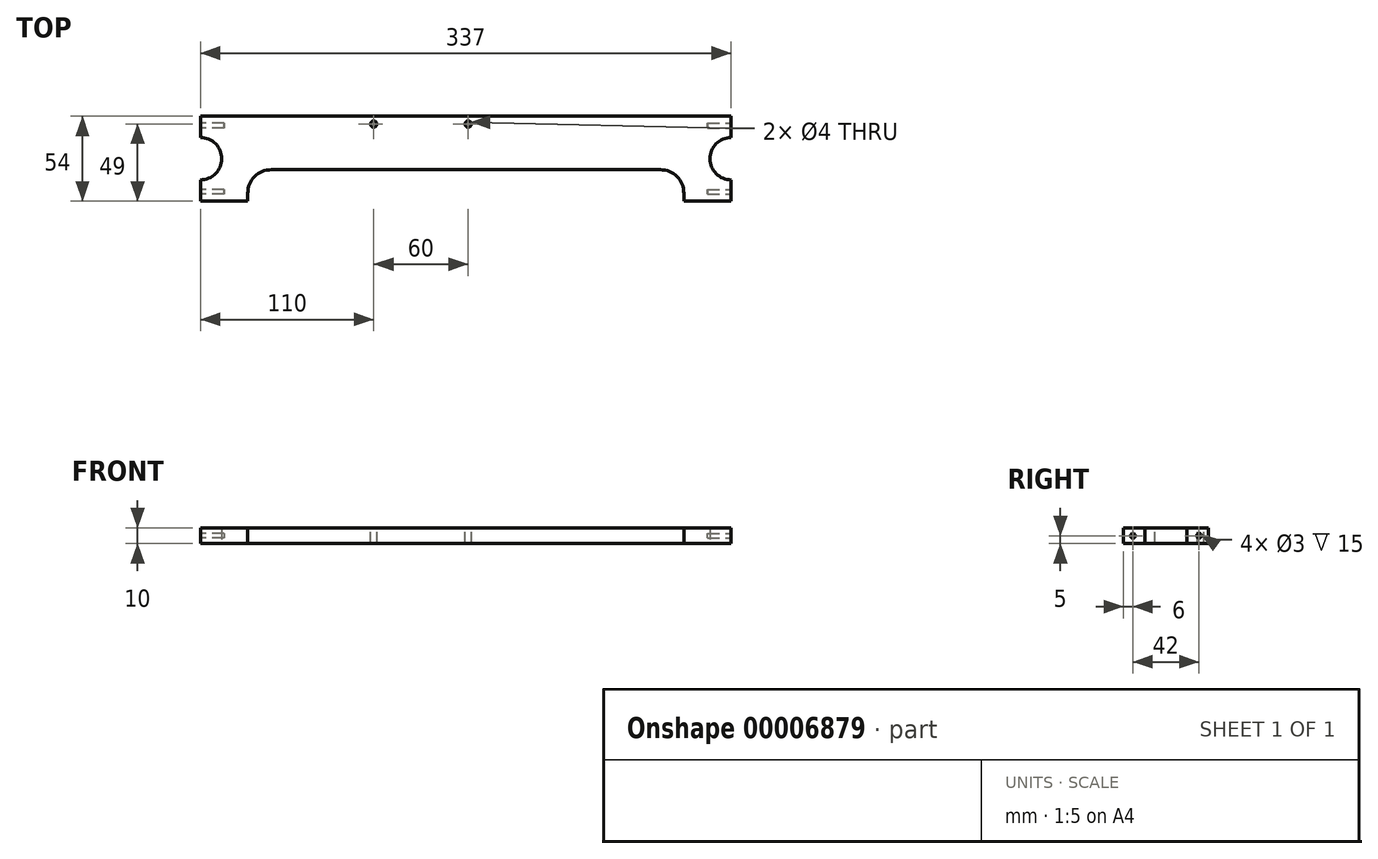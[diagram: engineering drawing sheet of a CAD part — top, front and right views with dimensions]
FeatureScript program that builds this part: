
annotation { "Feature Type Name" : "Feature", "Feature Type Description" : "" }
export const myFeature = defineFeature(function(context is Context, id is Id, definition is map)
    precondition{}
    {
        {
            var Q0;
            Q0=qCreatedBy(makeId("Top.planeOp"),FACE);
            var sketch = newSketch(context, id + "F0", { "sketchPlane" : qUnion([Q0])});
            skLineSegment(sketch, "E0.rect.bottom", {"start": v(164.95, -27) * mm, "end": v(-172.05, -27) * mm});
            skLineSegment(sketch, "E0.rect.top", {"start": v(164.95, 27) * mm, "end": v(-172.05, 27) * mm});
            skLineSegment(sketch, "E0.rect.left", {"start": v(164.95, -27) * mm, "end": v(164.95, 27) * mm});
            skLineSegment(sketch, "E0.rect.right", {"start": v(-172.05, -27) * mm, "end": v(-172.05, 27) * mm});
            skPoint(sketch, "E0.rect.middle", {"position": v(0, 0) * mm});
            skCircle(sketch, "E1", {"center": v(164.95, 0) * mm, "radius": 13.45 * mm});
            skCircle(sketch, "E2", {"center": v(-172.05, 0) * mm, "radius": 13.45 * mm});
            skSolve(sketch);
        }
        {
            var Q0;
            {var subQ8=sQuery(id+"F0.wireOp",EDGE,"E0.rect.bottom");Q0=makeQuery(id+"F0.imprint","IMPRINT",FACE,{"disambiguationData":[TD([[makeQuery(id+"F0.imprint","IMPRINT",EDGE,{"derivedFrom":subQ8}),-1.0]])]});}
            extrude(context, id + "F1", {"entities" : qUnion([Q0]), "depth" : (10) * mm});
        }
        {
            var Q0;
            Q0=makeQuery(id+"F1.opExtrude","CAP_FACE",FACE,{"disambiguationData":[OSD([sQuery(id+"F0.wireOp",EDGE,"E0.rect.bottom"),sQuery(id+"F0.wireOp",EDGE,"E0.rect.top"),sQuery(id+"F0.wireOp",EDGE,"E0.rect.left"),sQuery(id+"F0.wireOp",EDGE,"E0.rect.right"),sQuery(id+"F0.wireOp",EDGE,"E1"),sQuery(id+"F0.wireOp",EDGE,"E2")])],"isStart":false});
            var sketch = newSketch(context, id + "F2", { "sketchPlane" : qUnion([Q0])});
            skCircle(sketch, "E3", {"center": v(-62.05, 22) * mm, "radius": 2 * mm});
            skCircle(sketch, "E4", {"center": v(-2.05, 22) * mm, "radius": 2 * mm});
            skLineSegment(sketch, "E5", {"start": v(-127.05, -7) * mm, "end": v(119.95, -7) * mm});
            skLineSegment(sketch, "E6", {"start": v(134.95, -22) * mm, "end": v(134.95, -27) * mm});
            skLineSegment(sketch, "E7", {"start": v(-142.05, -27) * mm, "end": v(-142.05, -22) * mm});
            skPoint(sketch, "E8.visualSharp", {"position": v(-142.05, -7) * mm});
            skArc(sketch, "E8.filletArc", {"start": v(-127.05, -7) * mm, "mid": v(-137.66, -11.4) * mm, "end": v(-142.05, -22) * mm});
            skPoint(sketch, "E9.visualSharp", {"position": v(134.95, -7) * mm});
            skArc(sketch, "E9.filletArc", {"start": v(134.95, -22) * mm, "mid": v(130.56, -11.4) * mm, "end": v(119.95, -7) * mm});
            skSolve(sketch);
        }
        {
            var Q0;
            Q0 = qSketchRegion(id + "F2", true);
            extrude(context, id + "F3", {"entities" : qUnion([Q0]), "operationType" : NewBodyOperationType.REMOVE, "endBound" : BoundingType.THROUGH_ALL, "oppositeDirection" : true, "depth" : 25 * mm});
        }
        {
            var Q0;
            {var subQ0=sQuery(id+"F0.wireOp",EDGE,"E0.rect.left");Q0=makeQuery(id+"F1.opExtrude","SWEPT_FACE",FACE,{"disambiguationData":[OSD([subQ0]),TDD([makeQuery(id+"F0.imprint","IMPRINT",EDGE,{"disambiguationData":[TD([[makeQuery(id+"F0.imprint","INTERSECT",VERTEX,{"derivedFrom":[sQuery(id+"F0.wireOp",EDGE,"E0.rect.bottom"),subQ0]}),-1.0]])],"derivedFrom":subQ0})])]});}
            var sketch = newSketch(context, id + "F4", { "sketchPlane" : qUnion([Q0])});
            skLineSegment(sketch, "E10", {"start": v(-21, 10) * mm, "end": v(-21, 0) * mm, "construction": true});
            skCircle(sketch, "E11", {"center": v(-21, 5) * mm, "radius": 1.5 * mm});
            skSolve(sketch);
        }
        {
            var Q0;
            Q0 = qSketchRegion(id + "F4", true);
            extrude(context, id + "F5", {"entities" : qUnion([Q0]), "operationType" : NewBodyOperationType.REMOVE, "oppositeDirection" : true, "depth" : 15 * mm});
        }
        {
            var Q0;
            {var subQ0=sQuery(id+"F0.wireOp",EDGE,"E0.rect.left");Q0=makeQuery(id+"F1.opExtrude","SWEPT_FACE",FACE,{"disambiguationData":[OSD([subQ0]),TDD([makeQuery(id+"F0.imprint","IMPRINT",EDGE,{"disambiguationData":[TD([[makeQuery(id+"F0.imprint","INTERSECT",VERTEX,{"derivedFrom":[sQuery(id+"F0.wireOp",EDGE,"E0.rect.top"),subQ0]}),1.0]])],"derivedFrom":subQ0})])]});}
            var sketch = newSketch(context, id + "F6", { "sketchPlane" : qUnion([Q0])});
            skLineSegment(sketch, "E12", {"start": v(21, 10) * mm, "end": v(21, 0) * mm, "construction": true});
            skCircle(sketch, "E13", {"center": v(21, 5) * mm, "radius": 1.5 * mm});
            skSolve(sketch);
        }
        {
            var Q0;
            Q0 = qSketchRegion(id + "F6", true);
            extrude(context, id + "F7", {"entities" : qUnion([Q0]), "operationType" : NewBodyOperationType.REMOVE, "oppositeDirection" : true, "depth" : 15 * mm});
        }
        {
            var Q0;
            {var subQ0=sQuery(id+"F0.wireOp",EDGE,"E0.rect.right");Q0=makeQuery(id+"F1.opExtrude","SWEPT_FACE",FACE,{"disambiguationData":[OSD([subQ0]),TDD([makeQuery(id+"F0.imprint","IMPRINT",EDGE,{"disambiguationData":[TD([[makeQuery(id+"F0.imprint","INTERSECT",VERTEX,{"derivedFrom":[sQuery(id+"F0.wireOp",EDGE,"E0.rect.top"),subQ0]}),1.0]])],"derivedFrom":subQ0})])]});}
            var sketch = newSketch(context, id + "F8", { "sketchPlane" : qUnion([Q0])});
            skLineSegment(sketch, "E14", {"start": v(-21, 10) * mm, "end": v(-21, 0) * mm, "construction": true});
            skCircle(sketch, "E15", {"center": v(-21, 5) * mm, "radius": 1.5 * mm});
            skSolve(sketch);
        }
        {
            var Q0;
            Q0 = qSketchRegion(id + "F8", true);
            extrude(context, id + "F9", {"entities" : qUnion([Q0]), "operationType" : NewBodyOperationType.REMOVE, "oppositeDirection" : true, "depth" : 15 * mm});
        }
        {
            var Q0;
            {var subQ0=sQuery(id+"F0.wireOp",EDGE,"E0.rect.right");Q0=makeQuery(id+"F1.opExtrude","SWEPT_FACE",FACE,{"disambiguationData":[OSD([subQ0]),TDD([makeQuery(id+"F0.imprint","IMPRINT",EDGE,{"disambiguationData":[TD([[makeQuery(id+"F0.imprint","INTERSECT",VERTEX,{"derivedFrom":[sQuery(id+"F0.wireOp",EDGE,"E0.rect.bottom"),subQ0]}),-1.0]])],"derivedFrom":subQ0})])]});}
            var sketch = newSketch(context, id + "F10", { "sketchPlane" : qUnion([Q0])});
            skLineSegment(sketch, "E16", {"start": v(21, 10) * mm, "end": v(21, 0) * mm, "construction": true});
            skCircle(sketch, "E17", {"center": v(21, 5) * mm, "radius": 1.5 * mm});
            skSolve(sketch);
        }
        {
            var Q0;
            Q0 = qSketchRegion(id + "F10", true);
            extrude(context, id + "F11", {"entities" : qUnion([Q0]), "operationType" : NewBodyOperationType.REMOVE, "oppositeDirection" : true, "depth" : 15 * mm});
        }
        {
            var Q0;
            Q0=makeQuery(id+"F2.imprint","IMPRINT",FACE,{"disambiguationData":[TD([[makeQuery(id+"F2.imprint","IMPRINT",EDGE,{"derivedFrom":sQuery(id+"F2.wireOp",EDGE,"E5")}),-1.0]])]});
            extrude(context, id + "F12", {"entities" : qUnion([Q0]), "operationType" : NewBodyOperationType.REMOVE, "endBound" : BoundingType.THROUGH_ALL, "oppositeDirection" : true, "depth" : 25 * mm});
        }
    });
